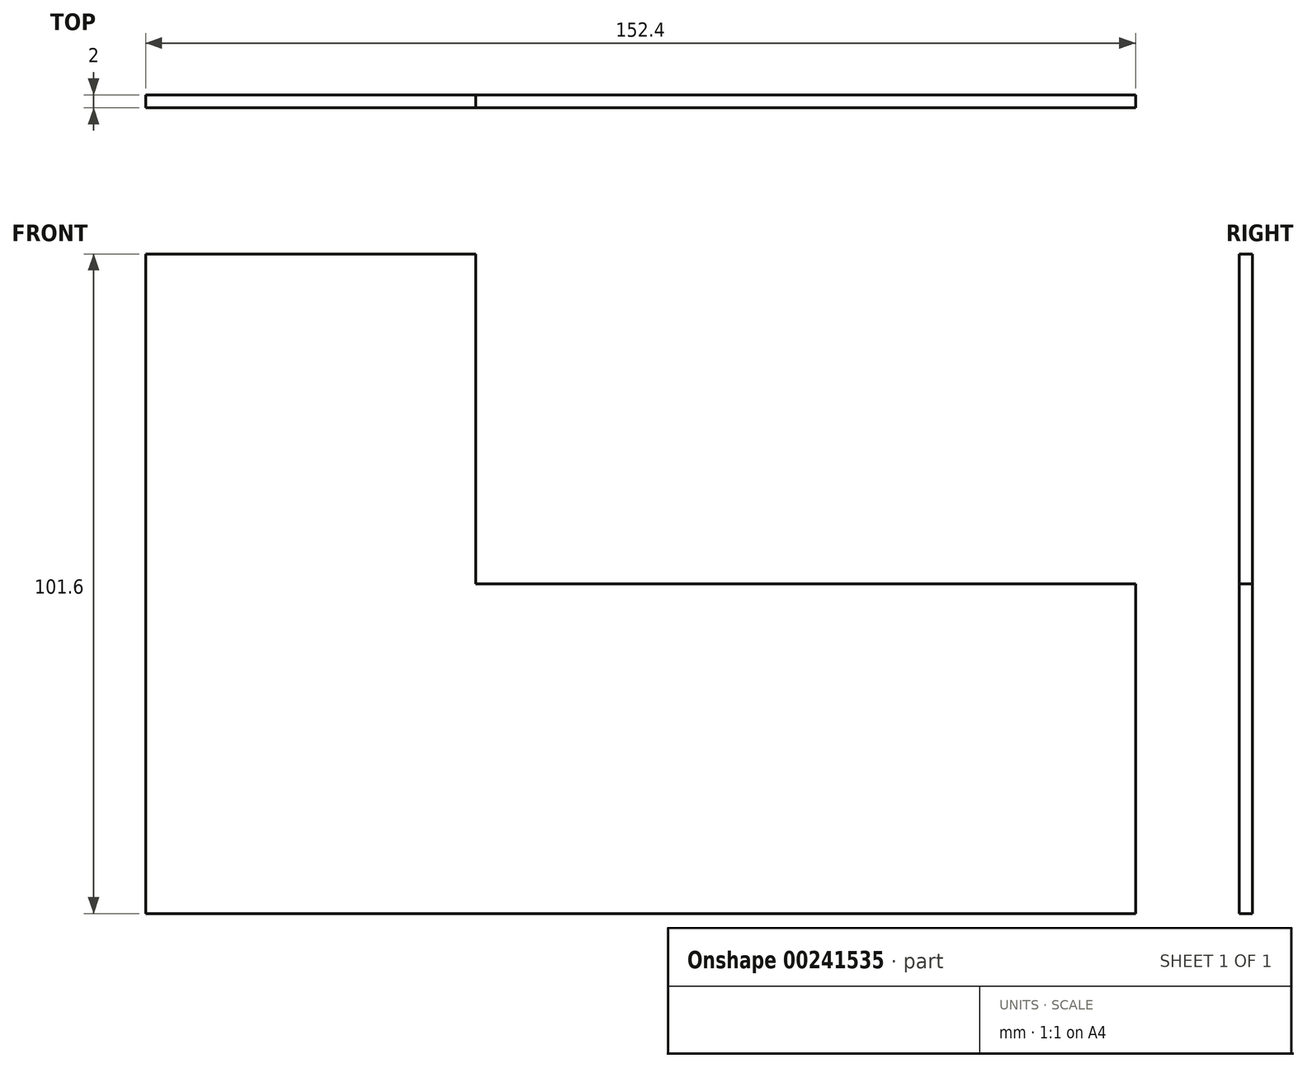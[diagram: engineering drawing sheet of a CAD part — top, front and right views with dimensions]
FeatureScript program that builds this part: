
annotation { "Feature Type Name" : "Feature", "Feature Type Description" : "" }
export const myFeature = defineFeature(function(context is Context, id is Id, definition is map)
    precondition{}
    {
        {
            assignVariable(context, id + "F0", {"name" : "C1", "anyValue" : 2});
        }
        {
            var Q0;
            Q0=qCreatedBy(makeId("Front.planeOp"),FACE);
            var sketch = newSketch(context, id + "F1", { "sketchPlane" : qUnion([Q0])});
            skLineSegment(sketch, "E0.bottom", {"start": v(-23.74, 24.95) * mm, "end": v(27.06, 24.95) * mm});
            skLineSegment(sketch, "E0.top", {"start": v(-23.74, -25.85) * mm, "end": v(27.06, -25.85) * mm});
            skLineSegment(sketch, "E0.left", {"start": v(-23.74, 24.95) * mm, "end": v(-23.74, -25.85) * mm});
            skLineSegment(sketch, "E0.right", {"start": v(27.06, 24.95) * mm, "end": v(27.06, -25.85) * mm});
            skSolve(sketch);
        }
        {
            var Q0;
            Q0 = qSketchRegion(id + "F1", true);
            extrude(context, id + "F2", {"entities" : qUnion([Q0]), "endBound" : BoundingType.SYMMETRIC, "depth" : (getVariable(context, 'C1')) * mm});
        }
        {
            var Q0;
            Q0=makeQuery(id+"F2.opExtrude","CAP_FACE",FACE,{"disambiguationData":[OSD([sQuery(id+"F1.wireOp",EDGE,"E0.bottom"),sQuery(id+"F1.wireOp",EDGE,"E0.top"),sQuery(id+"F1.wireOp",EDGE,"E0.left"),sQuery(id+"F1.wireOp",EDGE,"E0.right")])],"isStart":false});
            var sketch = newSketch(context, id + "F3", { "sketchPlane" : qUnion([Q0])});
            skLineSegment(sketch, "E1.bottom", {"start": v(-23.74, -25.85) * mm, "end": v(27.06, -25.85) * mm});
            skLineSegment(sketch, "E1.top", {"start": v(-23.74, -76.65) * mm, "end": v(27.06, -76.65) * mm});
            skLineSegment(sketch, "E1.left", {"start": v(-23.74, -25.85) * mm, "end": v(-23.74, -76.65) * mm});
            skLineSegment(sketch, "E1.right", {"start": v(27.06, -25.85) * mm, "end": v(27.06, -76.65) * mm});
            skSolve(sketch);
        }
        {
            var Q0;
            Q0 = qSketchRegion(id + "F3", true);
            extrude(context, id + "F4", {"entities" : qUnion([Q0]), "operationType" : NewBodyOperationType.ADD, "oppositeDirection" : true, "depth" : (getVariable(context, 'C1')) * mm});
        }
        {
            var Q0;
            Q0=makeQuery(id+"F4.boolean.opBoolean","MERGE",FACE,{"derivedFrom":[makeQuery(id+"F2.opExtrude","CAP_FACE",FACE,{"disambiguationData":[OSD([sQuery(id+"F1.wireOp",EDGE,"E0.bottom"),sQuery(id+"F1.wireOp",EDGE,"E0.top"),sQuery(id+"F1.wireOp",EDGE,"E0.left"),sQuery(id+"F1.wireOp",EDGE,"E0.right")])],"isStart":false}),makeQuery(id+"F4.opExtrude","CAP_FACE",FACE,{"disambiguationData":[OSD([sQuery(id+"F3.wireOp",EDGE,"E1.bottom"),sQuery(id+"F3.wireOp",EDGE,"E1.top"),sQuery(id+"F3.wireOp",EDGE,"E1.left"),sQuery(id+"F3.wireOp",EDGE,"E1.right")])],"isStart":true})]});
            var sketch = newSketch(context, id + "F5", { "sketchPlane" : qUnion([Q0])});
            skLineSegment(sketch, "E2.bottom", {"start": v(27.06, -76.65) * mm, "end": v(77.86, -76.65) * mm});
            skLineSegment(sketch, "E2.top", {"start": v(27.06, -25.85) * mm, "end": v(77.86, -25.85) * mm});
            skLineSegment(sketch, "E2.left", {"start": v(27.06, -76.65) * mm, "end": v(27.06, -25.85) * mm});
            skLineSegment(sketch, "E2.right", {"start": v(77.86, -76.65) * mm, "end": v(77.86, -25.85) * mm});
            skSolve(sketch);
        }
        {
            var Q0;
            Q0=makeQuery(id+"F5.imprint","IMPRINT",FACE,{"disambiguationData":[TD([[makeQuery(id+"F5.imprint","IMPRINT",EDGE,{"derivedFrom":sQuery(id+"F5.wireOp",EDGE,"E2.bottom")}),1.0]])]});
            extrude(context, id + "F6", {"entities" : qUnion([Q0]), "operationType" : NewBodyOperationType.ADD, "oppositeDirection" : true, "depth" : (getVariable(context, 'C1')) * mm});
        }
        {
            var Q0;
            Q0=makeQuery(id+"F6.boolean.opBoolean","MERGE",FACE,{"derivedFrom":[makeQuery(id+"F4.boolean.opBoolean","MERGE",FACE,{"derivedFrom":[makeQuery(id+"F2.opExtrude","CAP_FACE",FACE,{"disambiguationData":[OSD([sQuery(id+"F1.wireOp",EDGE,"E0.bottom"),sQuery(id+"F1.wireOp",EDGE,"E0.top"),sQuery(id+"F1.wireOp",EDGE,"E0.left"),sQuery(id+"F1.wireOp",EDGE,"E0.right")])],"isStart":false}),makeQuery(id+"F4.opExtrude","CAP_FACE",FACE,{"disambiguationData":[OSD([sQuery(id+"F3.wireOp",EDGE,"E1.bottom"),sQuery(id+"F3.wireOp",EDGE,"E1.top"),sQuery(id+"F3.wireOp",EDGE,"E1.left"),sQuery(id+"F3.wireOp",EDGE,"E1.right")])],"isStart":true})]}),makeQuery(id+"F6.opExtrude","CAP_FACE",FACE,{"disambiguationData":[OSD([sQuery(id+"F5.wireOp",EDGE,"E2.bottom"),sQuery(id+"F5.wireOp",EDGE,"E2.top"),sQuery(id+"F5.wireOp",EDGE,"E2.left"),sQuery(id+"F5.wireOp",EDGE,"E2.right")])],"isStart":true})]});
            var sketch = newSketch(context, id + "F7", { "sketchPlane" : qUnion([Q0])});
            skLineSegment(sketch, "E3.bottom", {"start": v(77.86, -76.65) * mm, "end": v(128.66, -76.65) * mm});
            skLineSegment(sketch, "E3.top", {"start": v(77.86, -25.85) * mm, "end": v(128.66, -25.85) * mm});
            skLineSegment(sketch, "E3.left", {"start": v(77.86, -76.65) * mm, "end": v(77.86, -25.85) * mm});
            skLineSegment(sketch, "E3.right", {"start": v(128.66, -76.65) * mm, "end": v(128.66, -25.85) * mm});
            skSolve(sketch);
        }
        {
            var Q0;
            Q0 = qSketchRegion(id + "F7", true);
            extrude(context, id + "F8", {"entities" : qUnion([Q0]), "operationType" : NewBodyOperationType.ADD, "oppositeDirection" : true, "depth" : (getVariable(context, 'C1')) * mm});
        }
    });
